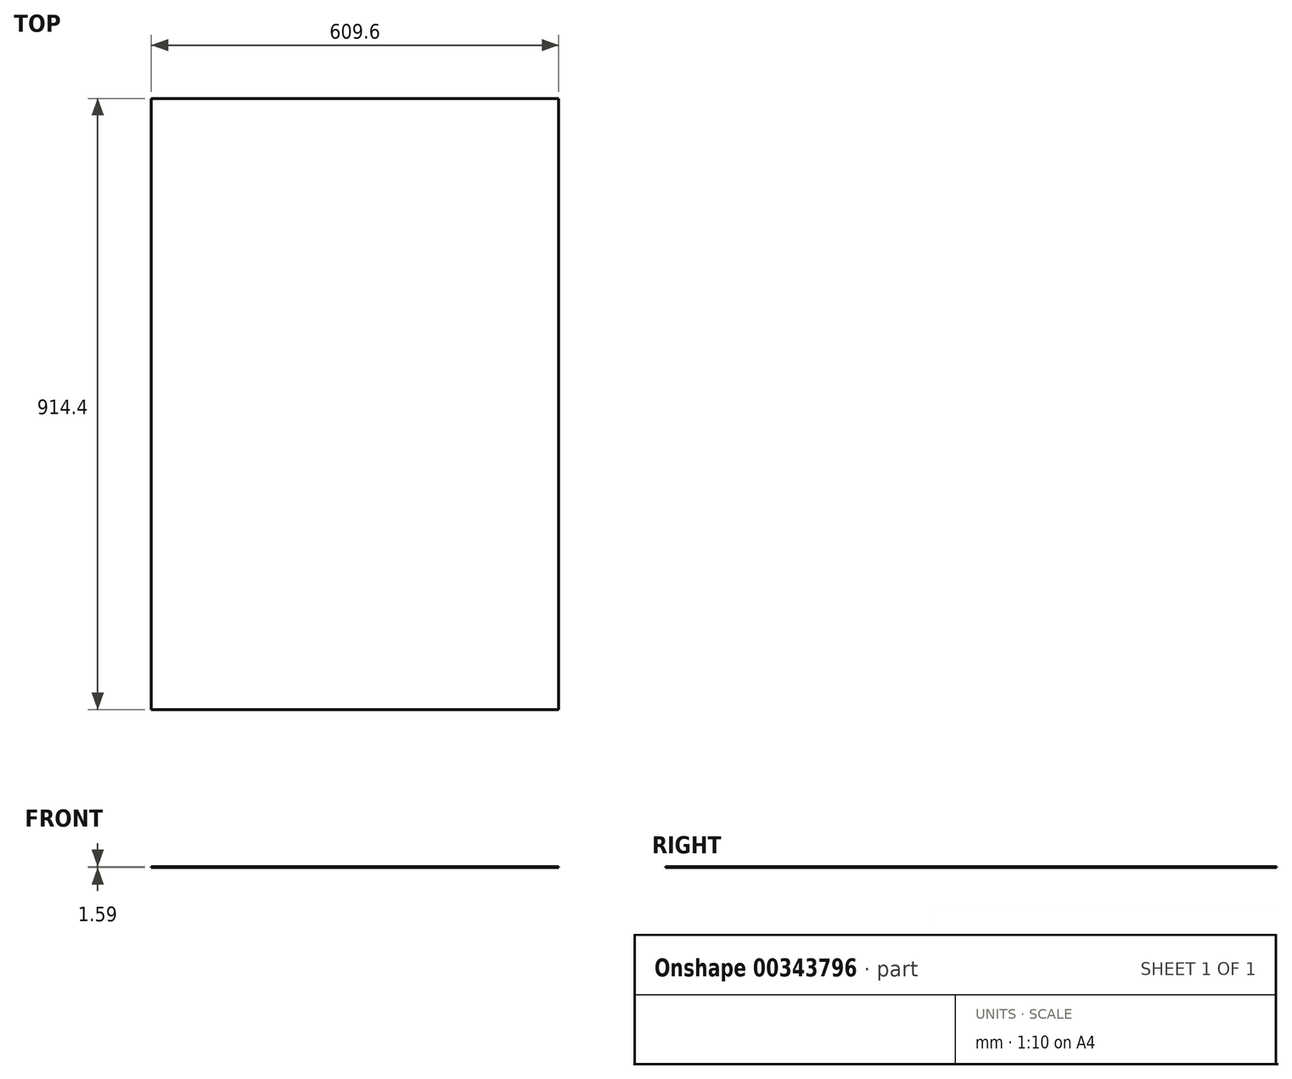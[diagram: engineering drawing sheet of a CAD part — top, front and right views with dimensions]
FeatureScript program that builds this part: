
annotation { "Feature Type Name" : "Feature", "Feature Type Description" : "" }
export const myFeature = defineFeature(function(context is Context, id is Id, definition is map)
    precondition{}
    {
        {
            var Q0;
            Q0=qCreatedBy(makeId("Top.planeOp"),FACE);
            var sketch = newSketch(context, id + "F0", { "sketchPlane" : qUnion([Q0])});
            skLineSegment(sketch, "E0.bottom", {"start": v(304.8, -457.2) * mm, "end": v(-304.8, -457.2) * mm});
            skLineSegment(sketch, "E0.top", {"start": v(304.8, 457.2) * mm, "end": v(-304.8, 457.2) * mm});
            skLineSegment(sketch, "E0.left", {"start": v(304.8, -457.2) * mm, "end": v(304.8, 457.2) * mm});
            skLineSegment(sketch, "E0.right", {"start": v(-304.8, -457.2) * mm, "end": v(-304.8, 457.2) * mm});
            skPoint(sketch, "E0.middle", {"position": v(0, 0) * mm});
            skSolve(sketch);
        }
        {
            var Q0;
            Q0=makeQuery(id+"F0.imprint","IMPRINT",FACE,{"disambiguationData":[TD([[makeQuery(id+"F0.imprint","IMPRINT",EDGE,{"derivedFrom":sQuery(id+"F0.wireOp",EDGE,"E0.bottom")}),-1.0]])]});
            extrude(context, id + "F1", {"entities" : qUnion([Q0]), "depth" : 1.59 * mm});
        }
    });
